# Revit family: Vitra_Plural_WallMountedBidet_7831B403-0288
name_source: partatom
category: Plumbing Fixtures
revit_build: Autodesk Revit 2017 (Build: 20160225_1515(x64)
units: mm (PartAtom-declared; Revit-internal decimal feet)

## family parameters
Cut with Voids When Loaded = No
Host = Face
OmniClass Number = 23.45.05.14.27
OmniClass Title = Bidets
Part Type = Normal
Room Calculation Point = No
Round Connector Dimension = Use Diameter
Shared = Yes

## types (5) — shared parameters
BIMobject category = Bidets
CW Connection = Yes
Default Elevation = 410 mm  [stored 1.34514 ft]
Description = VitrA Plural Wall Mounted Bidet
Design country = Turkey
HW Connection = Yes
IFC Classification = Sanitary Terminal
Main Material = Ceramic
Manufacturer = Vitra
Manufacturer name = Vitra
Masterformat 2014 Code = 22 41 13.19
Masterformat 2014 Description = Residential Bidets
MountingType = Wall Mounted
NBS Referans Code = 35-06-11
NBS Referans Description = Bidets
Nominal Depth (mm) = 548 mm
Nominal Height (mm) = 335 mm
Nominal Width (mm) = 361 mm
OmniClass Code = 23-31 23 00
OmniClass Description = Bidets
Product certification = https://vitraglobal.com
Product data url = https://www.vitra.com.tr
Product family = Plural
Product group = Wall Mounted Bidet
UNSPSC Code = 30181502
UNSPSC Description = Sanitary Ware
URL = https://www.vitra.com.tr
Uniclass 1.4 Code = L7215
Uniclass 1.4 Description = Bidets
Uniclass 2.0 Code = PR-35-06-11
Uniclass 2.0 Description = Bidets
Uniclass 2015 Code = Pr_40_20_06_11
Uniclass 2015 Name = Bidets
Uniformat II Code = C10
Uniformat II Description = Interior Construction
Vent Connection = No
Warranty Period (Year) = 10 Years
Waste Connection = Yes
Weight Net (kg) = 25,10
Youtube = https://www.youtube.com
zero-valued in all types: Cost

## per-type parameters (varying)
| type | Article No. (default) | Color | Model | Product SKU | Secondary Material |
| Bidet_WallMountedBidet_Vitra_Plural_(White)_7831B403-0288 | 7831B403-0288 | White | 7831B403-0288 | 7831B403-0288 | Vitra-Ceramic-White |
| Bidet_WallMountedBidet_Vitra_Plural_(MatteWhite)_7831B401-0288 | 7831B401-0288 | Matte White | 7831B401-0288 | 7831B401-0288 | Vitra-MatteWhite |
| Bidet_WallMountedBidet_Vitra_Plural_(MatteBeige)_7831B420-0288 | 7831B420-0288 | Matte Beige | 7831B420-0288 | 7831B420-0288 | Vitra-MatteBeige |
| Bidet_WallMountedBidet_Vitra_Plural_(MatteMink)_7831B450-0288 | 7831B450-0288 | Matte Mink | 7831B450-0288 | 7831B450-0288 | Vitra-MatteMink |
| Bidet_WallMountedBidet_Vitra_Plural_(MatteBlack)_7831B483-0288 | 7831B483-0288 | Matte Black | 7831B483-0288 | 7831B483-0288 | Vitra-MatteBlack |

note: [stored X ft] marks values corroborated as IEEE doubles in the binary element streams (Revit-internal decimal feet)

## geometry (parser evidence)
native form markers: Sweep x3
no freeform markers — native parametric forms only
